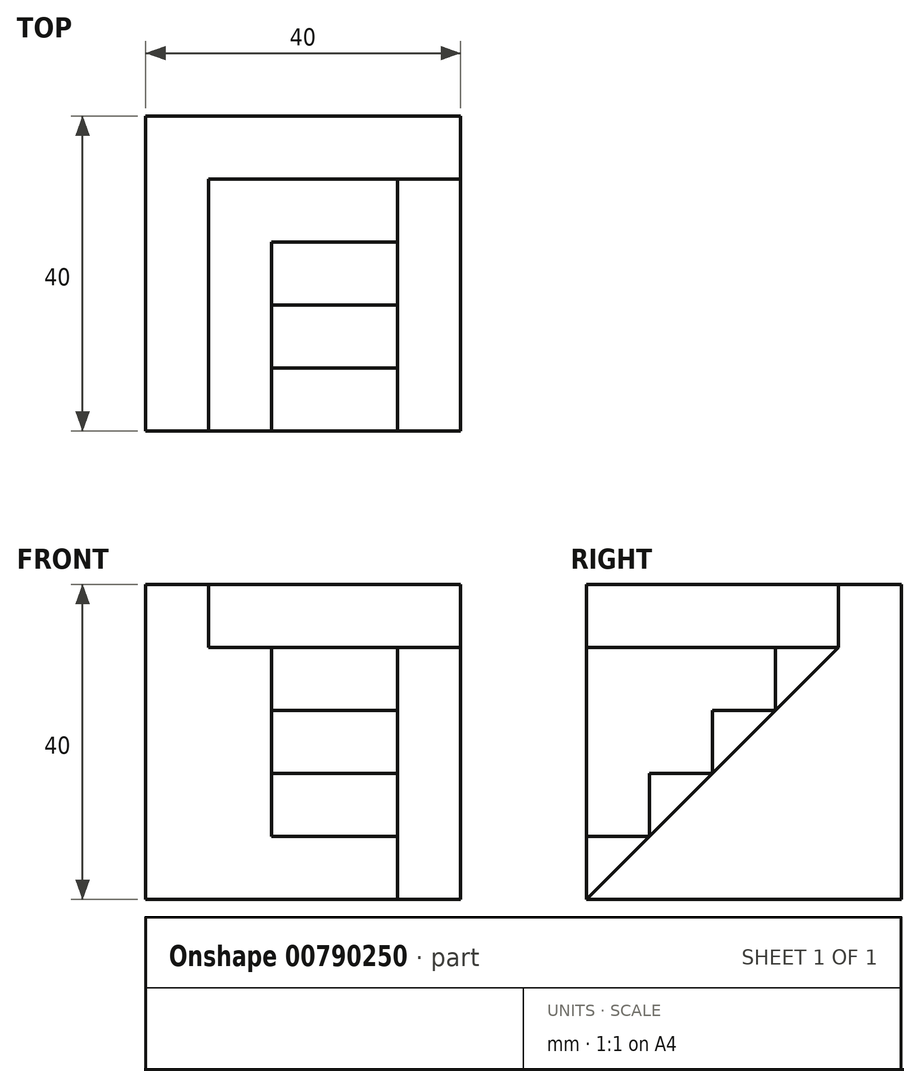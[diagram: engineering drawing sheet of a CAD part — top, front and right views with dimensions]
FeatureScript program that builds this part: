
annotation { "Feature Type Name" : "Feature", "Feature Type Description" : "" }
export const myFeature = defineFeature(function(context is Context, id is Id, definition is map)
    precondition{}
    {
        {
            var Q0;
            Q0=qCreatedBy(makeId("Top.planeOp"),FACE);
            var sketch = newSketch(context, id + "F0", { "sketchPlane" : qUnion([Q0])});
            skLineSegment(sketch, "E0.bottom", {"start": v(20, 20) * mm, "end": v(-20, 20) * mm});
            skLineSegment(sketch, "E0.top", {"start": v(20, -20) * mm, "end": v(-20, -20) * mm});
            skLineSegment(sketch, "E0.left", {"start": v(20, 20) * mm, "end": v(20, -20) * mm});
            skLineSegment(sketch, "E0.right", {"start": v(-20, 20) * mm, "end": v(-20, -20) * mm});
            skPoint(sketch, "E0.middle", {"position": v(0, 0) * mm});
            skLineSegment(sketch, "E1", {"start": v(-12, 12) * mm, "end": v(-12, -20) * mm});
            skLineSegment(sketch, "E2", {"start": v(-12, 12) * mm, "end": v(20, 12) * mm});
            skLineSegment(sketch, "E3", {"start": v(-4, -12) * mm, "end": v(12, -12) * mm});
            skLineSegment(sketch, "E4", {"start": v(-4, 4) * mm, "end": v(-4, -12) * mm});
            skLineSegment(sketch, "E5", {"start": v(12, 12) * mm, "end": v(12, -12) * mm});
            skLineSegment(sketch, "E6", {"start": v(-4, 4) * mm, "end": v(12, 4) * mm});
            skLineSegment(sketch, "E7", {"start": v(-4, -4) * mm, "end": v(12, -4) * mm});
            skPoint(sketch, "E8.orphan", {"position": v(20, -12) * mm});
            skLineSegment(sketch, "E9", {"start": v(12, -12) * mm, "end": v(12, -20) * mm});
            skLineSegment(sketch, "E10", {"start": v(-4, -12) * mm, "end": v(-4, -20) * mm});
            skPoint(sketch, "E10.endSnap0", {"position": v(0, -20) * mm});
            skSolve(sketch);
        }
        {
            var Q0;
            {var subQ8=sQuery(id+"F0.wireOp",EDGE,"E9");Q0=makeQuery(id+"F0.imprint","IMPRINT",FACE,{"disambiguationData":[TD([[makeQuery(id+"F0.imprint","IMPRINT",EDGE,{"derivedFrom":subQ8}),1.0]])]});}
            extrude(context, id + "F1", {"entities" : qUnion([Q0]), "depth" : 32 * mm, "offsetDistance" : 25 * mm});
        }
        {
            var Q0;
            Q0=makeQuery(id+"F1.opExtrude","SWEPT_FACE",FACE,{"disambiguationData":[OSD([sQuery(id+"F0.wireOp",EDGE,"E0.left")])]});
            var sketch = newSketch(context, id + "F2", { "sketchPlane" : qUnion([Q0])});
            skLineSegment(sketch, "E11", {"start": v(12, 32) * mm, "end": v(-20, 0) * mm});
            skSolve(sketch);
        }
        {
            var Q0;
            Q0=makeQuery(id+"F2.imprint","IMPRINT",FACE,{"disambiguationData":[TD([[makeQuery(id+"F2.imprint","IMPRINT",EDGE,{"derivedFrom":sQuery(id+"F2.wireOp",EDGE,"E11")}),-1.0]])]});
            extrude(context, id + "F3", {"entities" : qUnion([Q0]), "operationType" : NewBodyOperationType.REMOVE, "oppositeDirection" : true, "depth" : 25 * mm, "offsetDistance" : 25 * mm});
        }
        {
            var Q0;
            {var subQ4=sQuery(id+"F0.wireOp",EDGE,"E0.bottom");Q0=makeQuery(id+"F0.imprint","IMPRINT",FACE,{"disambiguationData":[TD([[makeQuery(id+"F0.imprint","IMPRINT",EDGE,{"derivedFrom":subQ4}),1.0]])]});}
            extrude(context, id + "F4", {"entities" : qUnion([Q0]), "operationType" : NewBodyOperationType.ADD, "depth" : 40 * mm, "offsetDistance" : 25 * mm});
        }
        {
            var Q0;
            {var subQ4=sQuery(id+"F0.wireOp",EDGE,"E1");Q0=makeQuery(id+"F0.imprint","IMPRINT",FACE,{"disambiguationData":[TD([[makeQuery(id+"F0.imprint","IMPRINT",EDGE,{"derivedFrom":subQ4}),1.0]])]});}
            extrude(context, id + "F5", {"entities" : qUnion([Q0]), "operationType" : NewBodyOperationType.ADD, "depth" : 32 * mm, "offsetDistance" : 25 * mm});
        }
        {
            var Q0;
            {var subQ0=sQuery(id+"F0.wireOp",EDGE,"E6");Q0=makeQuery(id+"F0.imprint","IMPRINT",FACE,{"disambiguationData":[TD([[makeQuery(id+"F0.imprint","IMPRINT",EDGE,{"derivedFrom":subQ0}),-1.0]])]});}
            extrude(context, id + "F6", {"entities" : qUnion([Q0]), "operationType" : NewBodyOperationType.ADD, "depth" : 24 * mm, "offsetDistance" : 25 * mm});
        }
        {
            var Q0;
            {var subQ0=sQuery(id+"F0.wireOp",EDGE,"E3");Q0=makeQuery(id+"F0.imprint","IMPRINT",FACE,{"disambiguationData":[TD([[makeQuery(id+"F0.imprint","IMPRINT",EDGE,{"derivedFrom":subQ0}),1.0]])]});}
            extrude(context, id + "F7", {"entities" : qUnion([Q0]), "operationType" : NewBodyOperationType.ADD, "depth" : 16 * mm, "offsetDistance" : 25 * mm});
        }
        {
            var Q0;
            Q0=makeQuery(id+"F0.imprint","IMPRINT",FACE,{"disambiguationData":[TD([[makeQuery(id+"F0.imprint","IMPRINT",EDGE,{"derivedFrom":sQuery(id+"F0.wireOp",EDGE,"E3")}),-1.0]])]});
            extrude(context, id + "F8", {"entities" : qUnion([Q0]), "operationType" : NewBodyOperationType.ADD, "depth" : 8 * mm, "offsetDistance" : 25 * mm});
        }
    });
